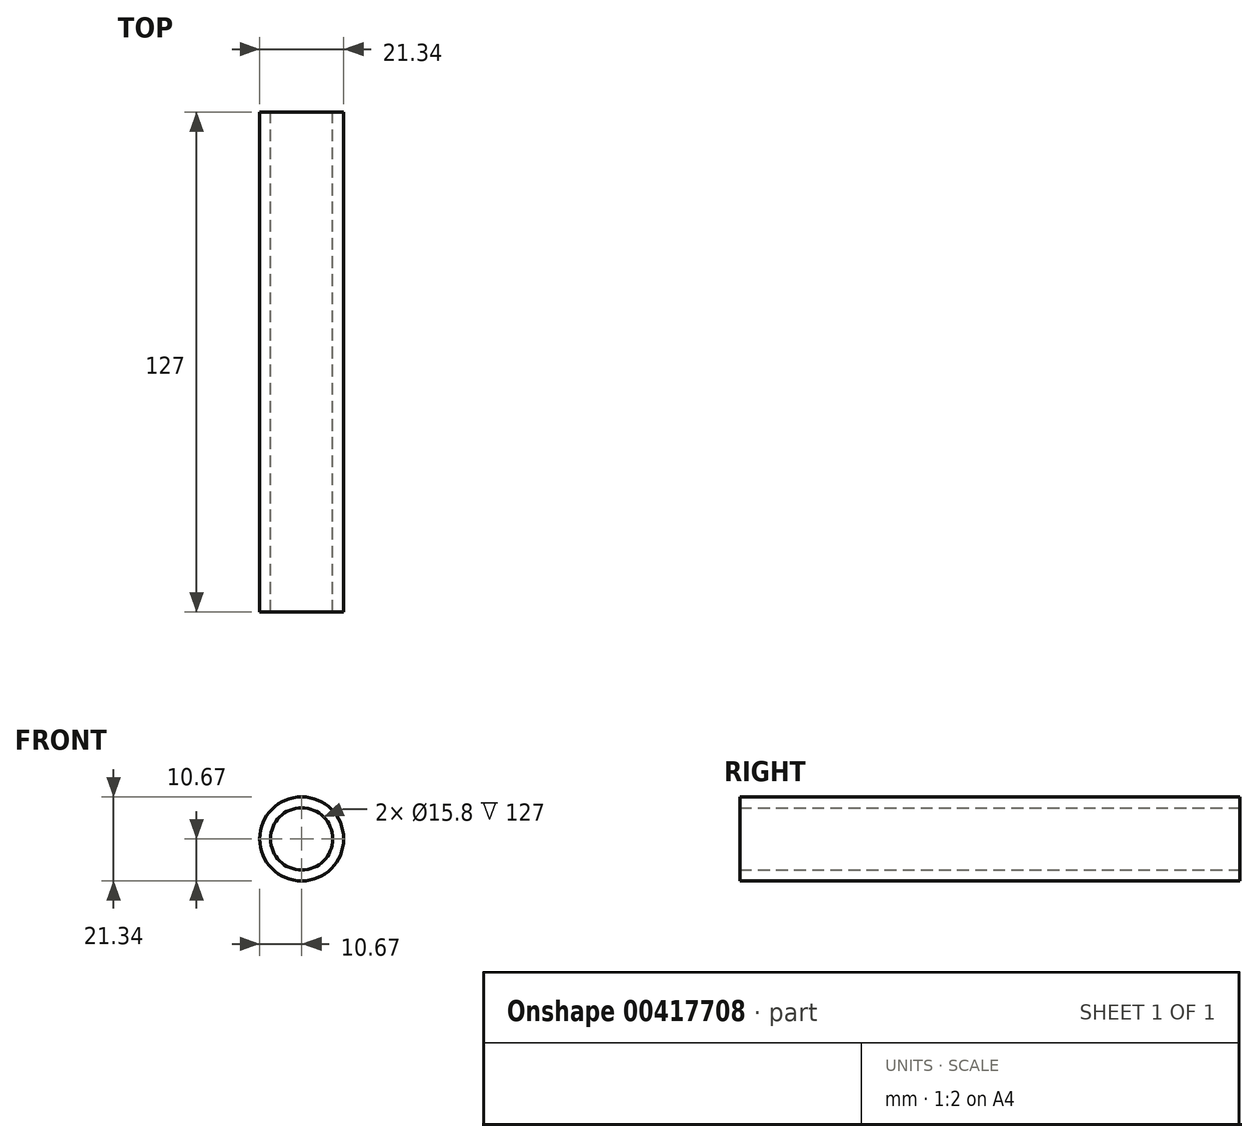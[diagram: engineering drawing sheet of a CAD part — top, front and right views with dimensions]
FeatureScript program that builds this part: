
annotation { "Feature Type Name" : "Feature", "Feature Type Description" : "" }
export const myFeature = defineFeature(function(context is Context, id is Id, definition is map)
    precondition{}
    {
        {
            var Q0;
            Q0=qCreatedBy(makeId("Front.planeOp"),FACE);
            var sketch = newSketch(context, id + "F0", { "sketchPlane" : qUnion([Q0])});
            skCircle(sketch, "E0", {"center": v(0, 0) * mm, "radius": 10.67 * mm});
            skCircle(sketch, "E1", {"center": v(0, 0) * mm, "radius": 7.9 * mm});
            skSolve(sketch);
        }
        {
            var Q0;
            Q0=makeQuery(id+"F0.imprint","IMPRINT",FACE,{"disambiguationData":[TD([[makeQuery(id+"F0.imprint","IMPRINT",EDGE,{"derivedFrom":sQuery(id+"F0.wireOp",EDGE,"E0")}),1.0]])]});
            extrude(context, id + "F1", {"entities" : qUnion([Q0]), "endBound" : BoundingType.SYMMETRIC, "depth" : 127 * mm});
        }
    });
